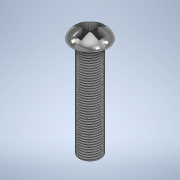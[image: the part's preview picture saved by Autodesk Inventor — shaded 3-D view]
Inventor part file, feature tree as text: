
AUTODESK INVENTOR PART (.ipt)
format: ipt  version: 2021 (Build 250183000, 183)  size: 1,078,272 bytes
history: native  units: in
note: dims shown in document units (in); Inventor stores cm internally (conversion verified against a paired STEP export)
features: sketch x5, extrude x2, plane x1, loft x1, helix x1, fillet x1, projected_geometry x1
ambient origin geometry x8: Origin, YZ Plane, XZ Plane, XY Plane, X Axis, Y Axis, Z Axis, Center Point
bodies: Solid1 (feature_tree)
feature tree (12):
  sketch  "Sketch3"  dims[d0=0.1969in d1=0.0591in]
  plane  "Work Plane1"
  loft  "Loft1"
  extrude  "Extrusion1"  Depth=0.3937in TaperAngle=90.0deg
  extrude  "Extrusion2"  Depth=0.0394in
  helix  "Coil1"  [1 undecoded]
  fillet  "Arredondamento1"  Radius=0.0394in
  sketch  "Sketch4"  dims[d2=0.0394in d3=0.3937in d4=90.0deg]
  sketch  "Sketch5"  dims[d5=0.0in d6=90.0deg d7=0.0394in d8=0.1378in d9=0.0394in]
  sketch  "Sketch6"  dims[d10=0.1378in]
  sketch  "Sketch8"  dims[d11=0.0472in d12=0.0in d13=0.1181in d14=0.5583in d15=0.0in d17=0.315in d18=0.5583in d19=17.7165in d20=0.0in d21=90.0deg d22=90.0deg d23=0.0in d24=0.0in d25=0.0079in]
  projected_geometry  "Projected Loop3"
note: 1 required parameter value undecoded (feature->parameter linkage not recoverable at this tier; creation-order binding heuristic only, values carry confidence <= 0.55)
